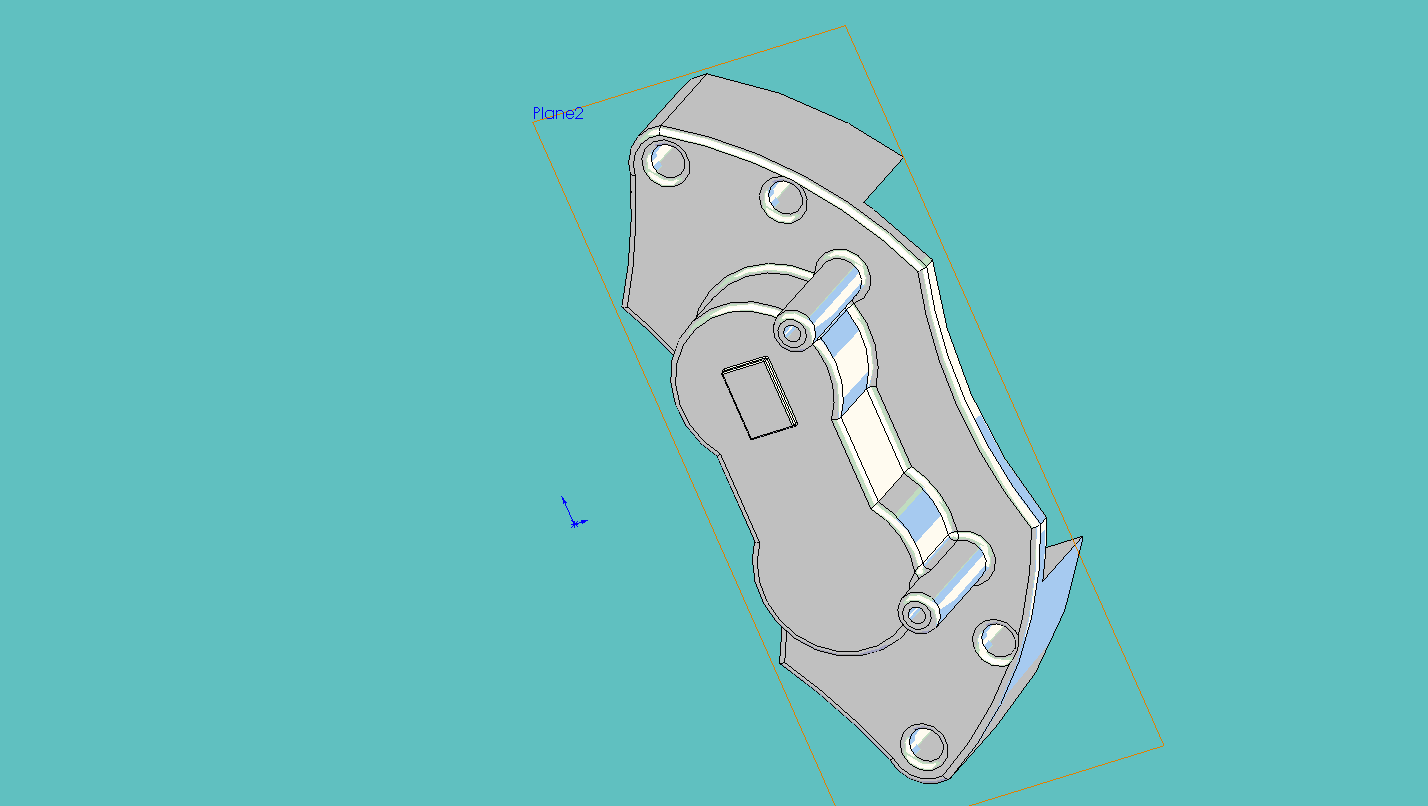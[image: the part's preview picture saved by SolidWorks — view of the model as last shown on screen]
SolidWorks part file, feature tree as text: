
SOLIDWORKS PART (.sldprt)
format: sldprt  version: not decoded by parser v0  size: 807,936 bytes
history: native  units: mm
features: sketch x10, cut_extrude x6, fillet x6, extrude x4, plane x2, material x1 (+13 scaffold rows collapsed)
feature tree (42):
  scaffold x13  (default folders/planes/origin — collapsed)
  material  "Material <not specified>"
  sketch  "Sketch1"  dims[D1=63.5mm]
  extrude  "Extrude1"  Depth=31.75mm
  sketch  "Sketch5"
  extrude  "Extrude2"  Depth=50.8mm
  sketch  "Sketch3"  dims[D1=50.0mm]
  cut_extrude  "Cut-Extrude1"  Depth=25.4mm
  sketch  "Sketch7"  dims[c1.D1=12.7mm c1.D2=12.7mm c2.D1=~13.906952mm c2.D2=25.0mm c2.D3=25.0mm c3.D1=~12.799272mm]
  cut_extrude  "Cut-Extrude2"  [1 undecoded]
  fillet  "Fillet1"  Radius=2.54mm
  fillet  "Fillet2"  Radius=2.54mm
  fillet  "Fillet3"  Radius=2.54mm
  sketch  "Sketch10"
  cut_extrude  "Cut-Extrude3"  [1 undecoded]
  plane  "Plane1"  Offset=10.16mm
  plane  "Plane2"  Offset=8.636mm
  sketch  "Sketch13"
  cut_extrude  "Cut-Extrude4"  [1 undecoded]
  sketch  "Sketch14"
  cut_extrude  "Cut-Extrude5"  [1 undecoded]
  sketch  "Sketch15"
  extrude  "Extrude3"  Depth=53.18mm
  fillet  "Fillet4"  Radius=2.54mm
  sketch  "Sketch16"  dims[D1=~1.636236mm]
  cut_extrude  "Cut-Extrude6"  Depth=27.94mm
  fillet  "Fillet5"  Radius=2.54mm
  sketch  "Sketch17"
  extrude  "Extrude4"  Depth=2.54mm
  fillet  "Fillet6"  Radius=0.508mm
decode coverage: 16 of 26 modeling features carry decoded parameters
note: ~ marks probable driven/reference dimensions
note: 4 parameter values undecoded
summary: no parameter record found for 4 features
note: suppression state not decoded; provenance and decode notes live in map.json
